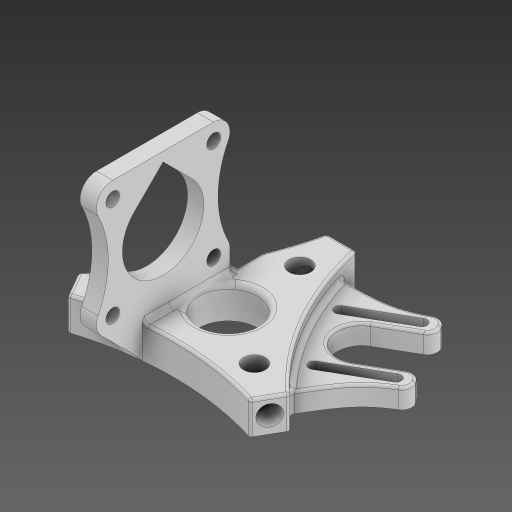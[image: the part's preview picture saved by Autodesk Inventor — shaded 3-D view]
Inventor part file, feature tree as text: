
AUTODESK INVENTOR PART (.ipt)
format: ipt  version: 2024 (Build 280153000, 153)  size: 608,256 bytes
history: native  units: mm
features: fillet x8, sketch x6, extrude x5, hole x3, plane x2, pattern_circular x1, projected_geometry x1
ambient origin geometry x8: Origin, YZ Plane, XZ Plane, XY Plane, X Axis, Y Axis, Z Axis, Center Point
bodies: Body1 (feature_tree)
feature tree (26):
  extrude  "Extrusion2"  Depth=6.65mm
  plane  "Work Plane3"
  sketch  "Sketch6"  dims[d14=30.0deg d15=30.0deg]
  extrude  "Extrusion3"  TaperAngle=30.0deg  [1 undecoded]
  hole  "Hole2"  [1 undecoded]
  plane  "Work Plane4"
  extrude  "Extrusion4"  Depth=17.0mm
  fillet  "Fillet1"  Radius=30.0mm
  fillet  "Fillet3"  Radius=10.0mm
  fillet  "Fillet8"  [1 undecoded]
  fillet  "Fillet9"  Radius=11.0mm
  fillet  "Fillet11"  Radius=22.0mm
  hole  "Hole5"  [1 undecoded]
  pattern_circular  "Circular Pattern2"  [2 undecoded]
  fillet  "Fillet13"  Radius=10.0mm
  sketch  "Sketch12"  dims[d44=25.0mm d45=31.0mm]
  extrude  "Extrusion5"  Depth=20.0mm
  extrude  "Extrusion6"  Depth=30.0mm
  hole  "Hole6"  [1 undecoded]
  fillet  "Fillet14"  Radius=5.0mm
  fillet  "Fillet15"  [1 undecoded]
  sketch  "Sketch2"  dims[d9=18.0mm d10=6.65mm]
  sketch  "Sketch8"  dims[d22=17.0mm d23=22.0mm]
  sketch  "Sketch11"  dims[d24=6.0mm d27=17.0mm d28=30.0mm d30=360.0deg d32=10.0mm d33=0.0mm d41=-9.0mm d42=11.0mm d43=22.0mm]
  sketch  "Sketch13"  dims[d46=31.0mm d48=5.0mm d49=10.0mm d50=20.0mm d52=31.0mm d53=20.0mm d55=31.0mm d58=30.0mm d60=30.0mm d61=5.0mm d62=0.0mm d70=4.2mm d71=6.0mm d72=8.2mm d73=2.0mm d74=90.0deg d75=8.0mm d76=0.0mm d77=-10.0mm d78=17.0mm d79=28.0mm d80=27.94mm d81=4.372mm d82=18.4mm d83=3.162mm d84=3.162mm d85=3.23mm d86=3.23mm d88=6.5mm d89=6.5mm d90=15.0mm d91=6.0mm d92=0.0mm d93=3.0mm d95=0.75mm d100=1.6mm d101=0.75mm d114=6.0mm d116=30.0mm d118=360.0deg d120=37.0mm d128=9.0mm d129=6.2mm d130=6.0mm d131=4.0mm d132=2.0mm d133=90.0deg d134=12.0mm d135=0.0mm d136=5.0mm d137=30.0mm d138=360.0deg d141=1.5mm d142=45.0deg d143=12.9mm d144=15.0mm d145=10.0mm d146=9.15mm d147=2.0mm d148=2.0mm d149=10.0mm d150=0.0mm d151=0.0mm d152=0.0mm d153=3.5mm d154=6.0mm d155=3.023mm d156=2.0mm d157=14.3117mm d158=15.0mm d159=0.0mm d160=3.1mm d161=5.0mm d162=6.5mm d163=0.8mm d164=11.0mm]
  projected_geometry  "Project Cut Edges1"
note: 8 required parameter values undecoded (feature->parameter linkage not recoverable at this tier; creation-order binding heuristic only, values carry confidence <= 0.55)
